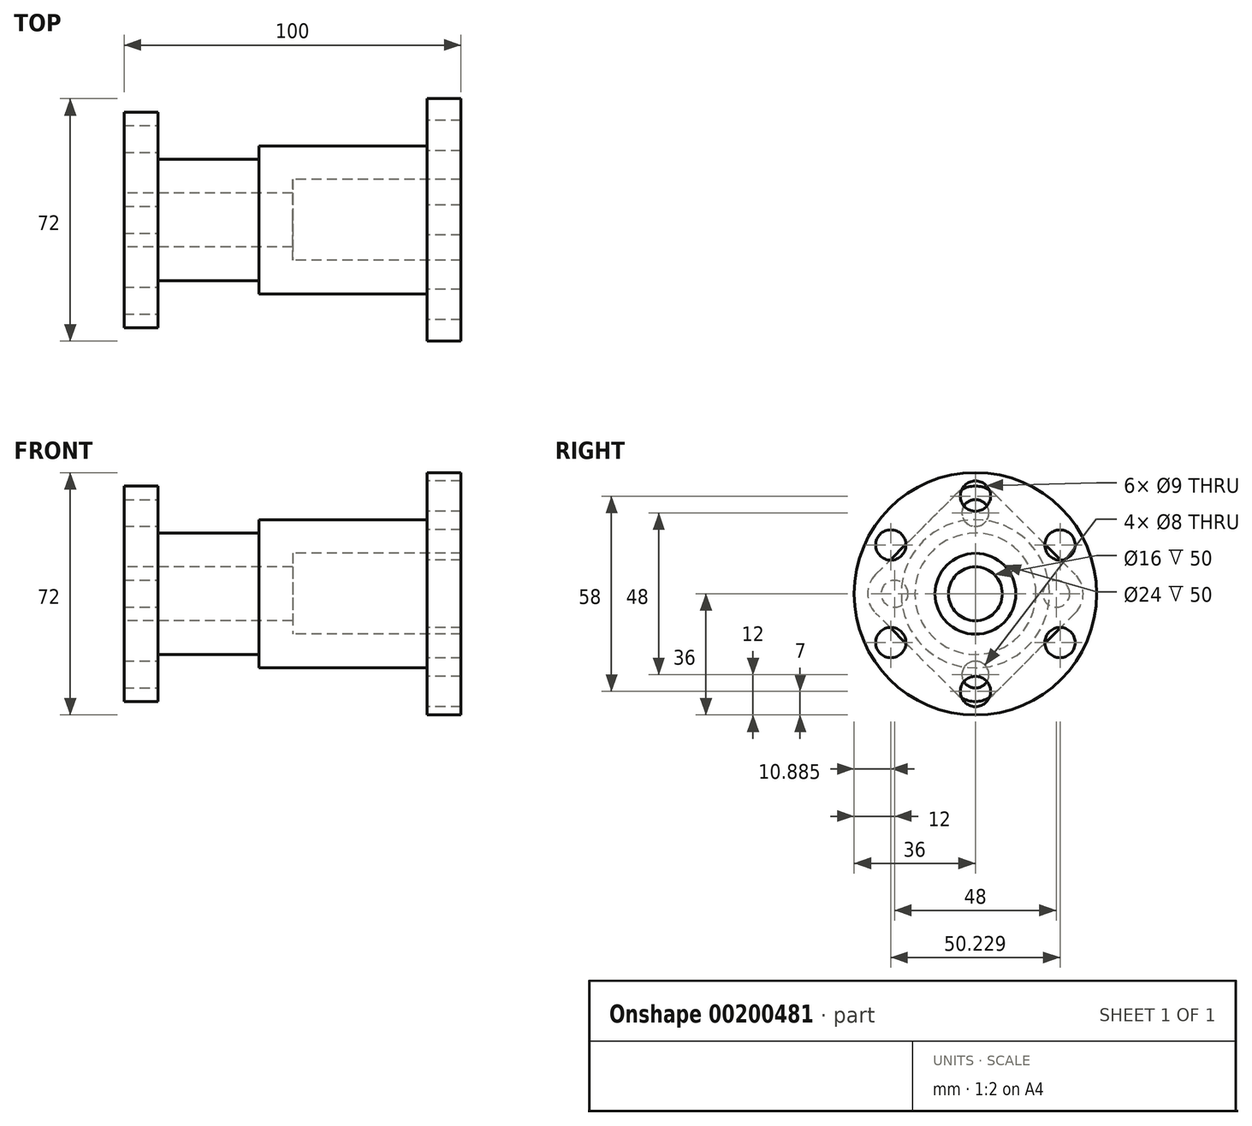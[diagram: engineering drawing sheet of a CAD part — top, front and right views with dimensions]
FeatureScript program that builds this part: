
annotation { "Feature Type Name" : "Feature", "Feature Type Description" : "" }
export const myFeature = defineFeature(function(context is Context, id is Id, definition is map)
    precondition{}
    {
        {
            var Q0;
            Q0=qCreatedBy(makeId("Front.planeOp"),FACE);
            var sketch = newSketch(context, id + "F0", { "sketchPlane" : qUnion([Q0])});
            skLineSegment(sketch, "E0", {"start": v(-18.2, 8) * mm, "end": v(-18.2, 18) * mm});
            skLineSegment(sketch, "E1", {"start": v(-18.2, 18) * mm, "end": v(11.8, 18) * mm});
            skLineSegment(sketch, "E2", {"start": v(11.8, 18) * mm, "end": v(11.8, 22) * mm});
            skLineSegment(sketch, "E3", {"start": v(11.8, 22) * mm, "end": v(61.8, 22) * mm});
            skLineSegment(sketch, "E4", {"start": v(61.8, 22) * mm, "end": v(61.8, 36) * mm});
            skLineSegment(sketch, "E5", {"start": v(61.8, 36) * mm, "end": v(71.8, 36) * mm});
            skLineSegment(sketch, "E6", {"start": v(71.8, 36) * mm, "end": v(71.8, 12) * mm});
            skLineSegment(sketch, "E7", {"start": v(-18.2, 8) * mm, "end": v(21.8, 8) * mm});
            skLineSegment(sketch, "E8", {"start": v(21.8, 8) * mm, "end": v(21.8, 12) * mm});
            skLineSegment(sketch, "E9", {"start": v(21.8, 12) * mm, "end": v(71.8, 12) * mm});
            skLineSegment(sketch, "E10", {"start": v(-41.22, 0) * mm, "end": v(90.56, 0) * mm, "construction": true});
            skSolve(sketch);
        }
        {
            var Q0;
            Q0=makeQuery(id+"F0.imprint","IMPRINT",FACE,{"disambiguationData":[TD([[makeQuery(id+"F0.imprint","IMPRINT",EDGE,{"derivedFrom":sQuery(id+"F0.wireOp",EDGE,"E0")}),-1.0]])]});
            var Q1;
            Q1=sQuery(id+"F0.wireOp",EDGE,"E10");
            revolve(context, id + "F1", {"entities" : qUnion([Q0]), "axis" : qUnion([Q1]), "revolveType" : RevolveType.FULL});
        }
        {
            var Q0;
            Q0=makeQuery(id+"F1.opRevolve","SWEPT_FACE",FACE,{"disambiguationData":[OSD([sQuery(id+"F0.wireOp",EDGE,"E4")])]});
            var sketch = newSketch(context, id + "F2", { "sketchPlane" : qUnion([Q0])});
            skCircle(sketch, "E11", {"center": v(0, 29) * mm, "radius": 4.5 * mm});
            skCircle(sketch, "E12.1.0", {"center": v(-25.11, 14.5) * mm, "radius": 4.5 * mm});
            skCircle(sketch, "E12.2.0", {"center": v(-25.11, -14.5) * mm, "radius": 4.5 * mm});
            skCircle(sketch, "E12.3.0", {"center": v(0, -29) * mm, "radius": 4.5 * mm});
            skCircle(sketch, "E12.4.0", {"center": v(25.11, -14.5) * mm, "radius": 4.5 * mm});
            skCircle(sketch, "E12.5.0", {"center": v(25.11, 14.5) * mm, "radius": 4.5 * mm});
            skPoint(sketch, "E12.center", {"position": v(0, 0) * mm});
            skSolve(sketch);
        }
        {
            var Q0;
            Q0 = qSketchRegion(id + "F2", true);
            extrude(context, id + "F3", {"entities" : qUnion([Q0]), "operationType" : NewBodyOperationType.REMOVE, "endBound" : BoundingType.THROUGH_ALL, "oppositeDirection" : true, "depth" : 25 * mm});
        }
        {
            var Q0;
            Q0=makeQuery(id+"F1.opRevolve","SWEPT_FACE",FACE,{"disambiguationData":[OSD([sQuery(id+"F0.wireOp",EDGE,"E0")])]});
            var sketch = newSketch(context, id + "F4", { "sketchPlane" : qUnion([Q0])});
            skLineSegment(sketch, "E13", {"start": v(-5.66, 29.66) * mm, "end": v(-29.66, 5.66) * mm});
            skLineSegment(sketch, "E14", {"start": v(-29.66, -5.66) * mm, "end": v(-5.66, -29.66) * mm});
            skLineSegment(sketch, "E15", {"start": v(5.66, -29.66) * mm, "end": v(29.66, -5.66) * mm});
            skLineSegment(sketch, "E16", {"start": v(29.66, 5.66) * mm, "end": v(5.66, 29.66) * mm});
            skCircle(sketch, "E17", {"center": v(0, 0) * mm, "radius": 8 * mm});
            skCircle(sketch, "E18", {"center": v(0, 24) * mm, "radius": 4 * mm});
            skPoint(sketch, "E19.visualSharp", {"position": v(0, 35.31) * mm});
            skArc(sketch, "E19.filletArc", {"start": v(5.66, 29.66) * mm, "mid": v(0, 32) * mm, "end": v(-5.66, 29.66) * mm});
            skCircle(sketch, "E20.1.0", {"center": v(-24, 0) * mm, "radius": 4 * mm});
            skArc(sketch, "E20.1.1", {"start": v(-29.66, 5.66) * mm, "mid": v(-32, 0) * mm, "end": v(-29.66, -5.66) * mm});
            skCircle(sketch, "E20.2.0", {"center": v(0, -24) * mm, "radius": 4 * mm});
            skArc(sketch, "E20.2.1", {"start": v(-5.66, -29.66) * mm, "mid": v(0, -32) * mm, "end": v(5.66, -29.66) * mm});
            skCircle(sketch, "E21.1.3.0", {"center": v(24, 0) * mm, "radius": 4 * mm});
            skArc(sketch, "E21.2.3.0", {"start": v(29.66, -5.66) * mm, "mid": v(32, 0) * mm, "end": v(29.66, 5.66) * mm});
            skPoint(sketch, "E22.orphan", {"position": v(35.31, 0) * mm});
            skPoint(sketch, "E23.orphan", {"position": v(0, -35.31) * mm});
            skPoint(sketch, "E24.orphan", {"position": v(-35.31, 0) * mm});
            skSolve(sketch);
        }
        {
            var Q0;
            Q0=makeQuery(id+"F4.imprint","IMPRINT",FACE,{"disambiguationData":[TD([[makeQuery(id+"F4.imprint","IMPRINT",EDGE,{"derivedFrom":sQuery(id+"F4.wireOp",EDGE,"E13")}),1.0]])]});
            var Q1;
            Q1=makeQuery(id+"F4.imprint","IMPRINT",FACE,{"disambiguationData":[TD([[makeQuery(id+"F4.imprint","IMPRINT",EDGE,{"derivedFrom":sQuery(id+"F4.wireOp",EDGE,"E17")}),-1.0]])]});
            extrude(context, id + "F5", {"entities" : qUnion([Q0, Q1]), "operationType" : NewBodyOperationType.ADD, "depth" : 10 * mm});
        }
    });
